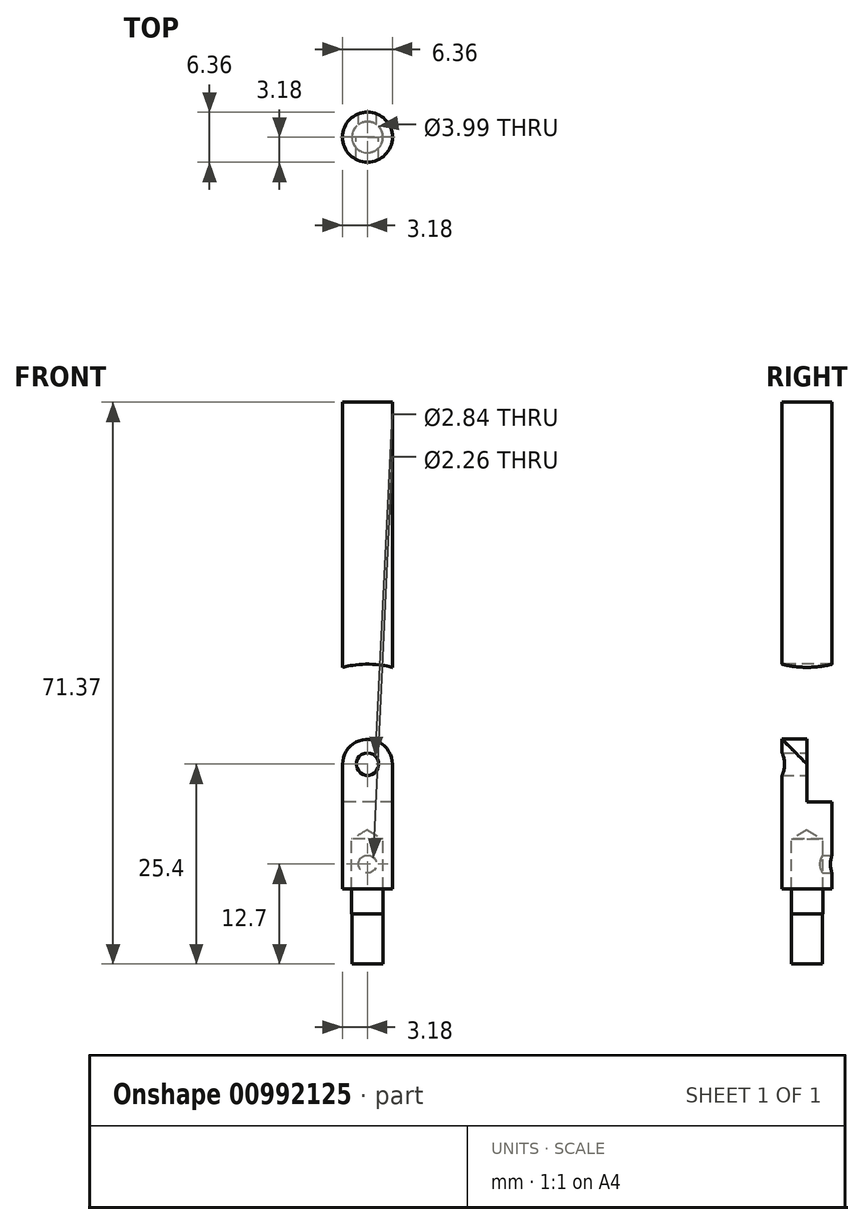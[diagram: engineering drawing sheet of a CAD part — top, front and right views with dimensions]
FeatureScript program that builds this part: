
annotation { "Feature Type Name" : "Feature", "Feature Type Description" : "" }
export const myFeature = defineFeature(function(context is Context, id is Id, definition is map)
    precondition{}
    {
        {
            var Q0;
            Q0=qCreatedBy(makeId("Front.planeOp"),FACE);
            var sketch = newSketch(context, id + "F0", { "sketchPlane" : qUnion([Q0])});
            skLineSegment(sketch, "E0", {"start": v(0, 22.69) * mm, "end": v(0, -22.84) * mm, "construction": true});
            skLineSegment(sketch, "E1.bottom", {"start": v(0, -4.83) * mm, "end": v(3.18, -4.83) * mm});
            skLineSegment(sketch, "E1.top", {"start": v(0, 45.97) * mm, "end": v(3.17, 45.97) * mm});
            skLineSegment(sketch, "E1.left", {"start": v(0, -4.83) * mm, "end": v(0, 45.97) * mm});
            skLineSegment(sketch, "E1.right", {"start": v(3.18, -4.83) * mm, "end": v(3.18, 45.97) * mm});
            skSolve(sketch);
        }
        {
            var Q0;
            Q0 = qSketchRegion(id + "F0", true);
            var Q1;
            Q1=sQuery(id+"F0.wireOp",EDGE,"E0");
            revolve(context, id + "F1", {"surfaceOperationType" : NewSurfaceOperationType.NEW, "entities" : qUnion([Q0]), "axis" : qUnion([Q1]), "revolveType" : RevolveType.FULL});
        }
        {
            var Q0;
            Q0=qCreatedBy(makeId("Front.planeOp"),FACE);
            var sketch = newSketch(context, id + "F2", { "sketchPlane" : qUnion([Q0])});
            skLineSegment(sketch, "E2.bottom", {"start": v(6.35, -4.83) * mm, "end": v(-6.35, -4.83) * mm});
            skLineSegment(sketch, "E2.top", {"start": v(6.35, 4.83) * mm, "end": v(-6.35, 4.83) * mm});
            skLineSegment(sketch, "E2.left", {"start": v(6.35, -4.83) * mm, "end": v(6.35, 4.83) * mm});
            skLineSegment(sketch, "E2.right", {"start": v(-6.35, -4.83) * mm, "end": v(-6.35, 4.83) * mm});
            skLineSegment(sketch, "E3", {"start": v(0, 0) * mm, "end": v(0, -4.83) * mm, "construction": true});
            skSolve(sketch);
        }
        {
            var Q0;
            Q0 = qSketchRegion(id + "F2", true);
            extrude(context, id + "F3", {"entities" : qUnion([Q0]), "operationType" : NewBodyOperationType.REMOVE, "endBound" : BoundingType.THROUGH_ALL, "depth" : 25.4 * mm, "offsetDistance" : 25.4 * mm});
        }
        {
            var Q0;
            Q0=qCreatedBy(makeId("Front.planeOp"),FACE);
            var sketch = newSketch(context, id + "F4", { "sketchPlane" : qUnion([Q0])});
            skCircle(sketch, "E4", {"center": v(0, 0) * mm, "radius": 1.42 * mm});
            skSolve(sketch);
        }
        {
            var Q0;
            Q0 = qSketchRegion(id + "F4", true);
            extrude(context, id + "F5", {"entities" : qUnion([Q0]), "operationType" : NewBodyOperationType.REMOVE, "endBound" : BoundingType.THROUGH_ALL, "oppositeDirection" : true, "depth" : 25.4 * mm, "offsetDistance" : 25.4 * mm});
        }
        {
            var Q0;
            Q0=qCreatedBy(makeId("Top.planeOp"),FACE);
            var sketch = newSketch(context, id + "F6", { "sketchPlane" : qUnion([Q0])});
            skLineSegment(sketch, "E5.bottom", {"start": v(-12.7, 6.35) * mm, "end": v(-3.18, 6.35) * mm});
            skLineSegment(sketch, "E5.top", {"start": v(-12.7, -6.35) * mm, "end": v(-3.18, -6.35) * mm});
            skLineSegment(sketch, "E5.left", {"start": v(-12.7, 6.35) * mm, "end": v(-12.7, -6.35) * mm});
            skLineSegment(sketch, "E5.right", {"start": v(-3.18, 6.35) * mm, "end": v(-3.18, -6.35) * mm});
            skLineSegment(sketch, "E6", {"start": v(0, 0) * mm, "end": v(-12.7, 0) * mm, "construction": true});
            skLineSegment(sketch, "E7", {"start": v(0, 0) * mm, "end": v(0, -6.35) * mm, "construction": true});
            skSolve(sketch);
        }
        {
            var Q0;
            Q0 = qSketchRegion(id + "F6", true);
            var Q1;
            Q1=sQuery(id+"F6.wireOp",EDGE,"E7");
            revolve(context, id + "F7", {"operationType" : NewBodyOperationType.REMOVE, "surfaceOperationType" : NewSurfaceOperationType.NEW, "entities" : qUnion([Q0]), "axis" : qUnion([Q1]), "revolveType" : RevolveType.ONE_DIRECTION, "angle" : 180 * degree});
        }
        {
            var Q0;
            Q0=qCreatedBy(makeId("Front.planeOp"),FACE);
            var sketch = newSketch(context, id + "F8", { "sketchPlane" : qUnion([Q0])});
            skLineSegment(sketch, "E8", {"start": v(0, 0) * mm, "end": v(0, -27.86) * mm, "construction": true});
            skLineSegment(sketch, "E9.bottom", {"start": v(0, -15.88) * mm, "end": v(3.18, -15.88) * mm});
            skLineSegment(sketch, "E9.top", {"start": v(0, 4.83) * mm, "end": v(3.17, 4.83) * mm});
            skLineSegment(sketch, "E9.left", {"start": v(0, -15.88) * mm, "end": v(0, 4.83) * mm});
            skLineSegment(sketch, "E9.right", {"start": v(3.18, -15.88) * mm, "end": v(3.18, 4.83) * mm});
            skSolve(sketch);
        }
        {
            var Q0;
            Q0 = qSketchRegion(id + "F8", true);
            var Q1;
            Q1=sQuery(id+"F8.wireOp",EDGE,"E8");
            revolve(context, id + "F9", {"surfaceOperationType" : NewSurfaceOperationType.NEW, "entities" : qUnion([Q0]), "axis" : qUnion([Q1]), "revolveType" : RevolveType.FULL});
        }
        {
            var Q0;
            Q0 = qSketchRegion(id + "F2", true);
            extrude(context, id + "F10", {"entities" : qUnion([Q0]), "operationType" : NewBodyOperationType.REMOVE, "endBound" : BoundingType.THROUGH_ALL, "oppositeDirection" : true, "depth" : 25.4 * mm, "offsetDistance" : 25.4 * mm});
        }
        {
            var Q0;
            Q0 = qSketchRegion(id + "F4", true);
            extrude(context, id + "F11", {"entities" : qUnion([Q0]), "operationType" : NewBodyOperationType.REMOVE, "endBound" : BoundingType.THROUGH_ALL, "depth" : 25.4 * mm, "offsetDistance" : 25.4 * mm});
        }
        {
            var Q0;
            Q0 = qSketchRegion(id + "F6", true);
            var Q1;
            Q1=sQuery(id+"F6.wireOp",EDGE,"E7");
            revolve(context, id + "F12", {"operationType" : NewBodyOperationType.REMOVE, "surfaceOperationType" : NewSurfaceOperationType.NEW, "entities" : qUnion([Q0]), "axis" : qUnion([Q1]), "revolveType" : RevolveType.ONE_DIRECTION, "oppositeDirection" : true, "angle" : 180 * degree});
        }
        {
            var Q0;
            Q0=makeQuery(id+"F9.opRevolve","SWEPT_FACE",FACE,{"disambiguationData":[OSD([sQuery(id+"F8.wireOp",EDGE,"E9.bottom")])]});
            var sketch = newSketch(context, id + "F13", { "sketchPlane" : qUnion([Q0])});
            skPoint(sketch, "E10", {"position": v(0, 0) * mm});
            skSolve(sketch);
        }
        {
            var Q0;
            Q0=sQuery(id+"F13.wireOp",VERTEX,"E10");
            var Q1;
            Q1=makeQuery(id+"F9.opRevolve","SWEPT_BODY",BODY,{"disambiguationData":[OSD([sQuery(id+"F8.wireOp",EDGE,"E9.bottom"),sQuery(id+"F8.wireOp",EDGE,"E9.top"),sQuery(id+"F8.wireOp",EDGE,"E9.left"),sQuery(id+"F8.wireOp",EDGE,"E9.right")])]});
            hole(context, id + "F14", {"style" : HoleStyle.SIMPLE, "endStyle" : HoleEndStyle.BLIND, "standardTappedOrClearance" : lookupTablePath({ "standard" : "ANSI", "size" : "#22 (0.16)", "type" : "Drilled" }), "standardBlindInLast" : lookupTablePath({ "standard" : "ANSI", "size" : "#22 (0.16)", "type" : "Drilled" }), "holeDiameter" : 4 * mm, "majorDiameter" : 2.84 * mm, "holeDepth" : 6.35 * mm, "isTappedThrough" : true, "tappedDepth" : 13.97 * mm, "tapClearance" : 5, "startFromSketch" : true, "locations" : qUnion([Q0]), "scope" : qUnion([Q1])});
        }
        {
            var Q0;
            Q0=qCreatedBy(makeId("Front.planeOp"),FACE);
            var sketch = newSketch(context, id + "F15", { "sketchPlane" : qUnion([Q0])});
            skPoint(sketch, "E11", {"position": v(0, -12.7) * mm});
            skSolve(sketch);
        }
        {
            var Q0;
            Q0=sQuery(id+"F15.wireOp",VERTEX,"E11");
            var Q1;
            Q1=makeQuery(id+"F9.opRevolve","SWEPT_BODY",BODY,{"disambiguationData":[OSD([sQuery(id+"F8.wireOp",EDGE,"E9.bottom"),sQuery(id+"F8.wireOp",EDGE,"E9.top"),sQuery(id+"F8.wireOp",EDGE,"E9.left"),sQuery(id+"F8.wireOp",EDGE,"E9.right")])]});
            hole(context, id + "F16", {"style" : HoleStyle.SIMPLE, "endStyle" : HoleEndStyle.THROUGH, "standardTappedOrClearance" : lookupTablePath({ "standard" : "ANSI", "engagement" : "75%", "pitch" : "40 tpi", "size" : "#4", "type" : "Tapped" }), "standardBlindInLast" : lookupTablePath({ "standard" : "ANSI", "fit" : "Normal", "engagement" : "75%", "pitch" : "40 tpi", "size" : "#4", "type" : "Clearance & tapped" }), "holeDiameter" : 2.26 * mm, "majorDiameter" : 2.84 * mm, "showTappedDepth" : true, "isTappedThrough" : true, "tappedDepth" : 13.97 * mm, "tapClearance" : 5, "startFromSketch" : true, "locations" : qUnion([Q0]), "scope" : qUnion([Q1])});
        }
        {
            var Q0;
            Q0=qCreatedBy(makeId("Front.planeOp"),FACE);
            var sketch = newSketch(context, id + "F17", { "sketchPlane" : qUnion([Q0])});
            skLineSegment(sketch, "E12", {"start": v(0, 0) * mm, "end": v(0, -39.76) * mm, "construction": true});
            skLineSegment(sketch, "E13.bottom", {"start": v(0, -25.4) * mm, "end": v(-1.96, -25.4) * mm});
            skLineSegment(sketch, "E13.top", {"start": v(0, -9.52) * mm, "end": v(-2, -9.52) * mm});
            skLineSegment(sketch, "E13.left", {"start": v(0, -25.4) * mm, "end": v(0, -9.52) * mm});
            skLineSegment(sketch, "E13.right", {"start": v(-2, -19.03) * mm, "end": v(-2, -9.52) * mm});
            skLineSegment(sketch, "E14", {"start": v(-2, -19.03) * mm, "end": v(-1.96, -19.05) * mm});
            skLineSegment(sketch, "E15", {"start": v(-1.96, -19.05) * mm, "end": v(-1.96, -25.4) * mm});
            skSolve(sketch);
        }
        {
            var Q0;
            Q0 = qSketchRegion(id + "F17", true);
            var Q1;
            Q1=sQuery(id+"F17.wireOp",EDGE,"E12");
            revolve(context, id + "F18", {"surfaceOperationType" : NewSurfaceOperationType.NEW, "entities" : qUnion([Q0]), "axis" : qUnion([Q1]), "revolveType" : RevolveType.FULL});
        }
    });
